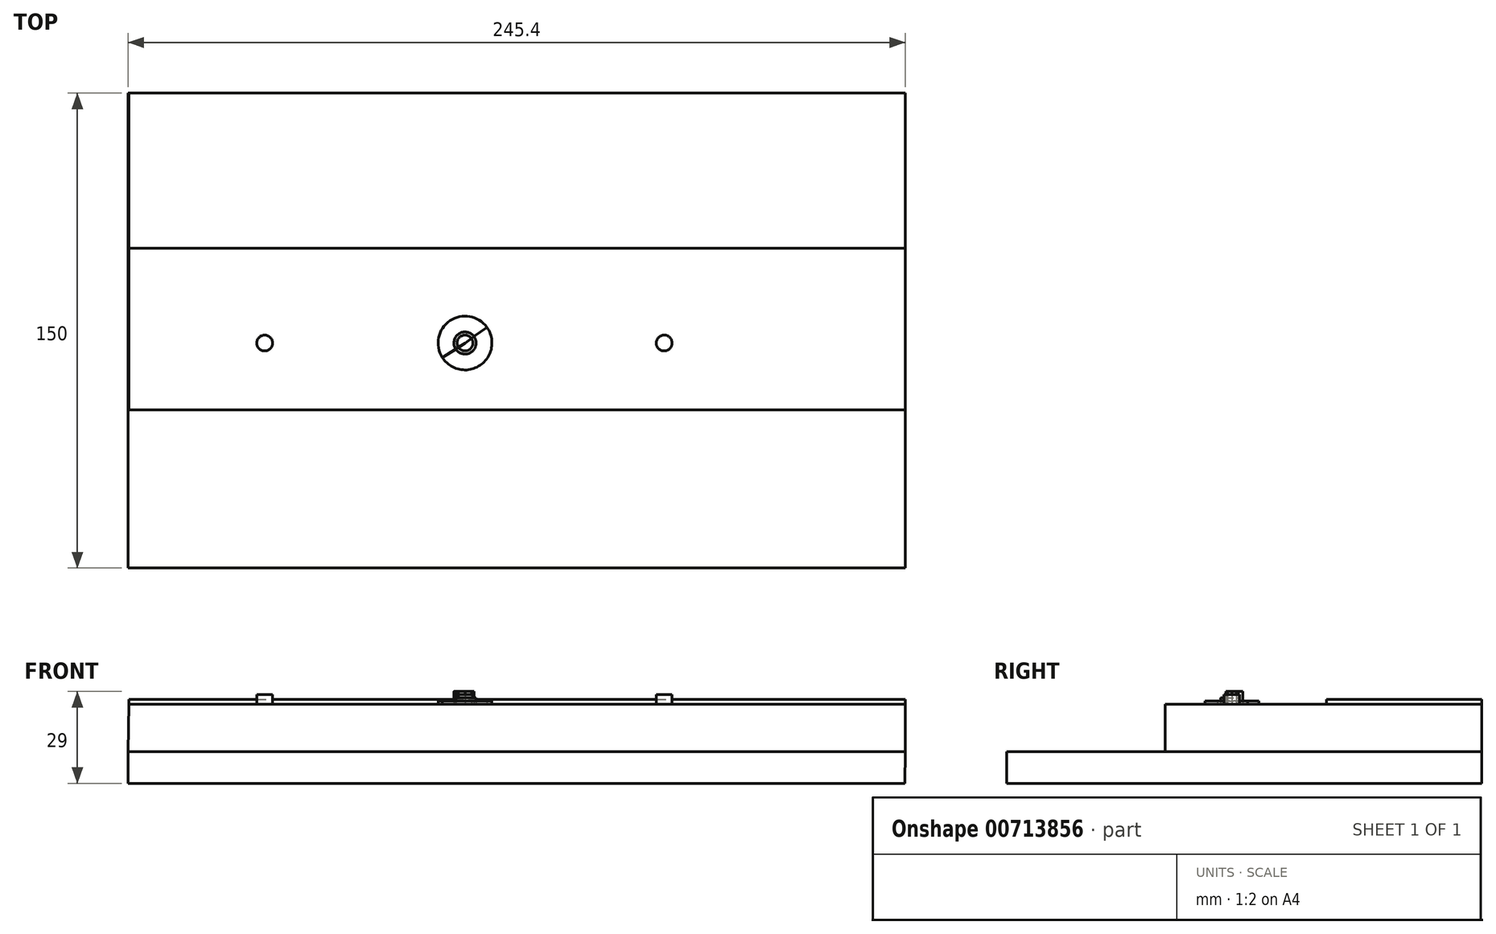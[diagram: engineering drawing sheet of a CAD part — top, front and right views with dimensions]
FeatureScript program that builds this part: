
annotation { "Feature Type Name" : "Feature", "Feature Type Description" : "" }
export const myFeature = defineFeature(function(context is Context, id is Id, definition is map)
    precondition{}
    {
        {
            var Q0;
            Q0=qCreatedBy(makeId("Front.planeOp"),FACE);
            var sketch = newSketch(context, id + "F0", { "sketchPlane" : qUnion([Q0])});
            skLineSegment(sketch, "E0", {"start": v(-43.05, 16) * mm, "end": v(-21.76, 16) * mm});
            skLineSegment(sketch, "E1", {"start": v(20.95, 16) * mm, "end": v(42.24, 16) * mm});
            skLineSegment(sketch, "E2", {"start": v(84.95, 16) * mm, "end": v(106.24, 16) * mm});
            skLineSegment(sketch, "E3", {"start": v(148.95, 16) * mm, "end": v(170.24, 16) * mm});
            skLineSegment(sketch, "E4", {"start": v(-75.16, 16) * mm, "end": v(170.24, 16) * mm});
            skLineSegment(sketch, "E5", {"start": v(170.24, 31) * mm, "end": v(-74.91, 31) * mm});
            skLineSegment(sketch, "E6", {"start": v(-74.91, 31) * mm, "end": v(-75.16, 16) * mm});
            skLineSegment(sketch, "E7", {"start": v(170.24, 31) * mm, "end": v(170.24, 16) * mm});
            skLineSegment(sketch, "E8", {"start": v(-74.91, 31) * mm, "end": v(-74.91, 32.5) * mm});
            skLineSegment(sketch, "E9", {"start": v(-74.91, 32.5) * mm, "end": v(170.2, 32.5) * mm});
            skLineSegment(sketch, "E10", {"start": v(170.2, 32.5) * mm, "end": v(170.24, 31) * mm});
            skLineSegment(sketch, "E11", {"start": v(-75.16, 16) * mm, "end": v(-75.16, 6) * mm});
            skLineSegment(sketch, "E12", {"start": v(-75.16, 6) * mm, "end": v(170.16, 6) * mm});
            skLineSegment(sketch, "E13", {"start": v(170.16, 6) * mm, "end": v(170.24, 16) * mm});
            skSolve(sketch);
        }
        {
            var Q0;
            {var subQ6=sQuery(id+"F0.wireOp",EDGE,"E11");Q0=makeQuery(id+"F0.imprint","IMPRINT",FACE,{"disambiguationData":[TD([[makeQuery(id+"F0.imprint","IMPRINT",EDGE,{"derivedFrom":subQ6}),1.0]])]});}
            extrude(context, id + "F1", {"entities" : qUnion([Q0]), "depth" : 150 * mm});
        }
        {
            var Q0;
            Q0=makeQuery(id+"F0.imprint","IMPRINT",FACE,{"disambiguationData":[TD([[makeQuery(id+"F0.imprint","IMPRINT",EDGE,{"derivedFrom":sQuery(id+"F0.wireOp",EDGE,"E5")}),1.0]])]});
            extrude(context, id + "F2", {"entities" : qUnion([Q0]), "depth" : 100 * mm});
        }
        {
            var Q0;
            Q0=makeQuery(id+"F0.imprint","IMPRINT",FACE,{"disambiguationData":[TD([[makeQuery(id+"F0.imprint","IMPRINT",EDGE,{"derivedFrom":sQuery(id+"F0.wireOp",EDGE,"E5")}),-1.0]])]});
            extrude(context, id + "F3", {"entities" : qUnion([Q0]), "depth" : 49 * mm});
        }
        {
            var Q0;
            Q0=makeQuery(id+"F2.opExtrude","SWEPT_FACE",FACE,{"disambiguationData":[OSD([sQuery(id+"F0.wireOp",EDGE,"E5")])]});
            var sketch = newSketch(context, id + "F4", { "sketchPlane" : qUnion([Q0])});
            skCircle(sketch, "E14", {"center": v(-32, -78.93) * mm, "radius": 2.5 * mm});
            skCircle(sketch, "E15", {"center": v(31.24, -78.93) * mm, "radius": 2.5 * mm});
            skCircle(sketch, "E16", {"center": v(94.13, -78.93) * mm, "radius": 2.5 * mm});
            skCircle(sketch, "E17.0", {"center": v(31.24, -78.93) * mm, "radius": 3.5 * mm});
            skCircle(sketch, "E18.0", {"center": v(31.24, -78.93) * mm, "radius": 8.5 * mm});
            skLineSegment(sketch, "E19", {"start": v(31.24, -78.93) * mm, "end": v(29.17, -80.32) * mm});
            skLineSegment(sketch, "E20", {"start": v(29.17, -80.32) * mm, "end": v(28.35, -80.9) * mm});
            skLineSegment(sketch, "E21", {"start": v(28.35, -80.9) * mm, "end": v(24.08, -83.5) * mm});
            skLineSegment(sketch, "E22", {"start": v(24.08, -83.5) * mm, "end": v(31.24, -78.93) * mm});
            skLineSegment(sketch, "E23", {"start": v(33.27, -77.47) * mm, "end": v(31.24, -78.93) * mm});
            skLineSegment(sketch, "E24", {"start": v(33.27, -77.47) * mm, "end": v(34.06, -76.86) * mm});
            skLineSegment(sketch, "E25", {"start": v(34.06, -76.86) * mm, "end": v(38.14, -73.96) * mm});
            skSolve(sketch);
        }
        {
            var Q0;
            Q0=makeQuery(id+"F4.imprint","IMPRINT",FACE,{"disambiguationData":[TD([[makeQuery(id+"F4.imprint","IMPRINT",EDGE,{"derivedFrom":sQuery(id+"F4.wireOp",EDGE,"E16")}),1.0]])]});
            extrude(context, id + "F5", {"entities" : qUnion([Q0]), "depth" : 3 * mm});
        }
        {
            var Q0;
            Q0=makeQuery(id+"F4.imprint","IMPRINT",FACE,{"disambiguationData":[TD([[makeQuery(id+"F4.imprint","IMPRINT",EDGE,{"derivedFrom":sQuery(id+"F4.wireOp",EDGE,"E14")}),1.0]])]});
            extrude(context, id + "F6", {"entities" : qUnion([Q0]), "depth" : 3 * mm});
        }
        {
            var Q0;
            {var subQ0=sQuery(id+"F4.wireOp",EDGE,"E19");Q0=makeQuery(id+"F4.imprint","IMPRINT",FACE,{"disambiguationData":[TD([[makeQuery(id+"F4.imprint","IMPRINT",EDGE,{"derivedFrom":subQ0}),1.0]])]});}
            extrude(context, id + "F7", {"entities" : qUnion([Q0]), "depth" : 3 * mm});
        }
        {
            var Q0;
            {var subQ0=sQuery(id+"F4.wireOp",EDGE,"E23");Q0=makeQuery(id+"F4.imprint","IMPRINT",FACE,{"disambiguationData":[TD([[makeQuery(id+"F4.imprint","IMPRINT",EDGE,{"derivedFrom":subQ0}),-1.0]])]});}
            extrude(context, id + "F8", {"entities" : qUnion([Q0]), "depth" : 4 * mm});
        }
        {
            var Q0;
            {var subQ0=sQuery(id+"F4.wireOp",EDGE,"E24");Q0=makeQuery(id+"F4.imprint","IMPRINT",FACE,{"disambiguationData":[TD([[makeQuery(id+"F4.imprint","IMPRINT",EDGE,{"derivedFrom":subQ0}),1.0]])]});}
            extrude(context, id + "F9", {"entities" : qUnion([Q0]), "depth" : 4 * mm});
        }
        {
            var Q0;
            {var subQ0=sQuery(id+"F4.wireOp",EDGE,"E20");Q0=makeQuery(id+"F4.imprint","IMPRINT",FACE,{"disambiguationData":[TD([[makeQuery(id+"F4.imprint","IMPRINT",EDGE,{"derivedFrom":subQ0}),1.0]])]});}
            extrude(context, id + "F10", {"entities" : qUnion([Q0]), "depth" : 2 * mm});
        }
        {
            var Q0;
            {var subQ0=sQuery(id+"F4.wireOp",EDGE,"E25");Q0=makeQuery(id+"F4.imprint","IMPRINT",FACE,{"disambiguationData":[TD([[makeQuery(id+"F4.imprint","IMPRINT",EDGE,{"derivedFrom":subQ0}),1.0]])]});}
            extrude(context, id + "F11", {"entities" : qUnion([Q0]), "depth" : 1 * mm});
        }
        {
            var Q0;
            {var subQ0=sQuery(id+"F4.wireOp",EDGE,"E21");Q0=makeQuery(id+"F4.imprint","IMPRINT",FACE,{"disambiguationData":[TD([[makeQuery(id+"F4.imprint","IMPRINT",EDGE,{"derivedFrom":subQ0}),1.0]])]});}
            extrude(context, id + "F12", {"entities" : qUnion([Q0]), "depth" : 1 * mm});
        }
    });
